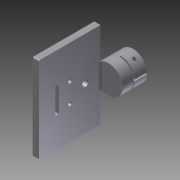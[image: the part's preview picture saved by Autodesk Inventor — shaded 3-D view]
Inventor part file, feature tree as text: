
AUTODESK INVENTOR PART (.ipt)
format: ipt  version: 2011 (Build 150239000, 239)  size: 186,368 bytes
history: native  units: mm
features: extrude x9, sketch x9, plane x5, fillet x3
ambient origin geometry x8: Origin, YZ Plane, XZ Plane, XY Plane, X Axis, Y Axis, Z Axis, Center Point
bodies: Volumenkörper1 (feature_tree)
feature tree (26):
  plane  "Arbeitsebene10"
  extrude  "Achshalter"  Depth=20.0mm TaperAngle=0.0deg
  plane  "Arbeitsebene11"
  extrude  "Extrusion11"  Depth=2.2mm
  plane  "Arbeitsebene2"
  extrude  "Extrusion12"  Depth=1.0mm TaperAngle=0.0deg
  plane  "Arbeitsebene16"
  extrude  "Extrusion13"  Depth=2.5mm
  plane  "Arbeitsebene17"
  extrude  "Extrusion14"  Depth=50.0mm TaperAngle=0.0deg
  extrude  "Extrusion16"  Depth=70.0mm
  fillet  "Rundung11"  Radius=2.0mm
  fillet  "Rundung12"  Radius=1.0mm
  fillet  "Rundung13"  Radius=1.0mm
  extrude  "Extrusion17"  Depth=21.0mm
  extrude  "Extrusion18"  Depth=10.0mm TaperAngle=0.0deg
  extrude  "Extrusion19"  Depth=14.5mm
  sketch  "Skizze7"  dims[d32=23.0mm d33=20.0mm d34=0.0mm]
  sketch  "Skizze16"  dims[d54=5.2mm d55=2.2mm]
  sketch  "Skizze17"  dims[d56=18.0mm d57=0.0mm d59=1.0mm d60=0.0mm]
  sketch  "Skizze18"  dims[d63=1.0mm d64=0.5mm d65=0.0mm d66=0.0mm d67=2.5mm]
  sketch  "Skizze19"  dims[d68=35.0mm d69=0.0mm d81=50.0mm d82=0.0mm]
  sketch  "Skizze23"  dims[d84=5.0mm d85=70.0mm d86=2.0mm d87=1.0mm d88=1.0mm]
  sketch  "Skizze24"  dims[d89=11.5mm d90=21.0mm]
  sketch  "Skizze25"  dims[d91=3.0mm d92=10.0mm d93=0.0mm]
  sketch  "Skizze26"  dims[d94=21.0mm d95=14.5mm d96=3.0mm d97=2.5mm d98=2.5mm d99=3.0mm d100=2.5mm d101=2.5mm d102=10.0mm d103=0.0mm d104=5.0mm d105=10.0mm d106=0.0mm]
